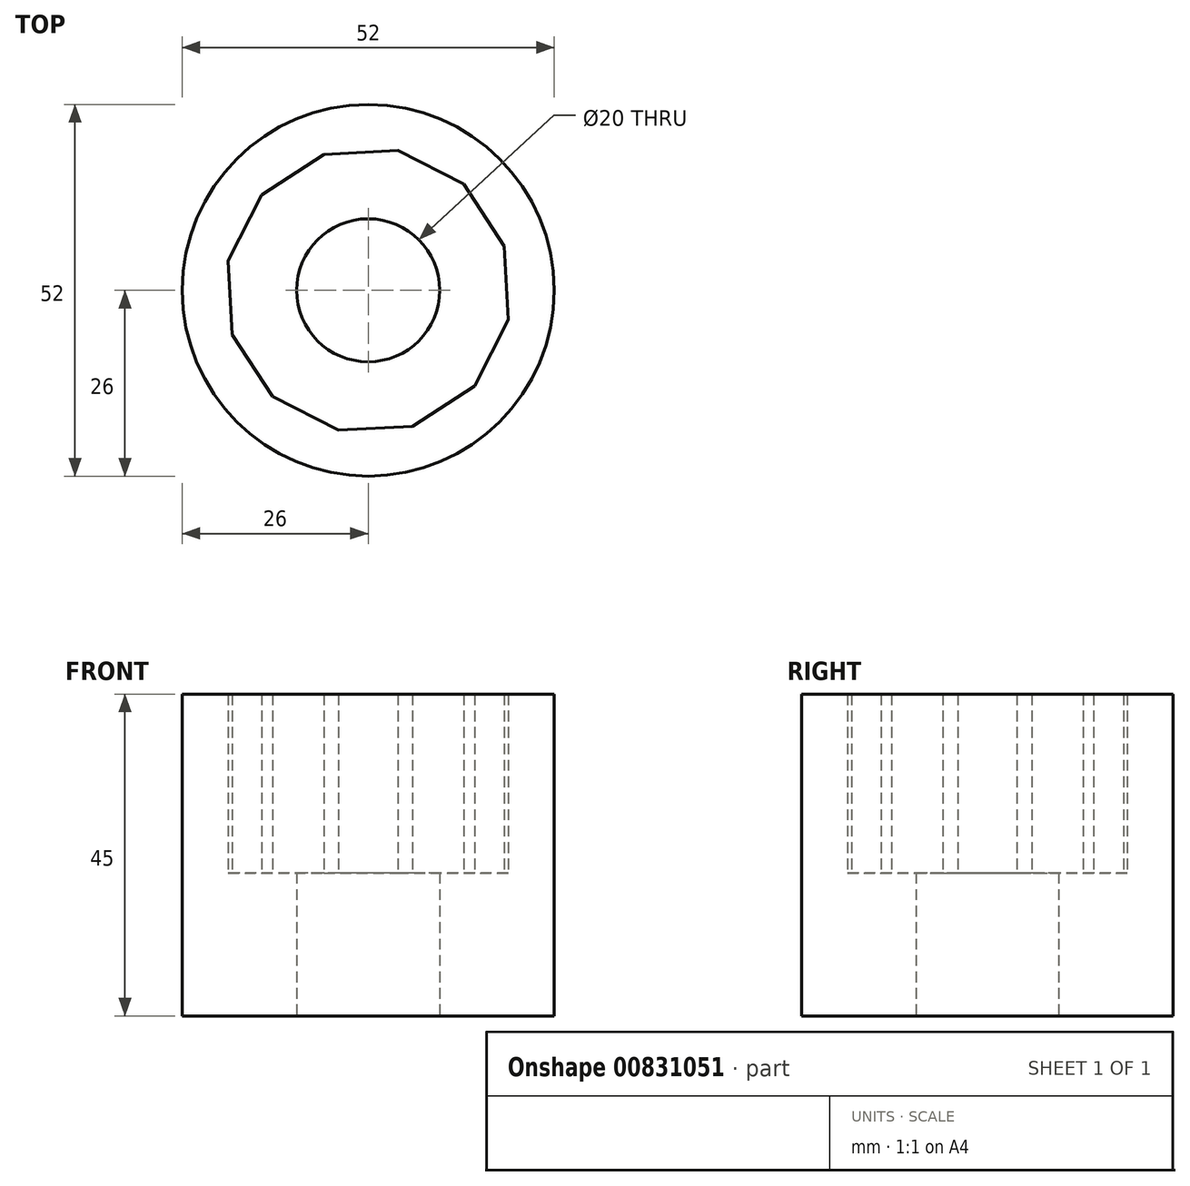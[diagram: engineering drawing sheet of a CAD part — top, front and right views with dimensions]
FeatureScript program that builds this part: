
annotation { "Feature Type Name" : "Feature", "Feature Type Description" : "" }
export const myFeature = defineFeature(function(context is Context, id is Id, definition is map)
    precondition{}
    {
        {
            var Q0;
            Q0=qCreatedBy(makeId("Top.planeOp"),FACE);
            var sketch = newSketch(context, id + "F0", { "sketchPlane" : qUnion([Q0])});
            skCircle(sketch, "E0", {"center": v(0, 0) * mm, "radius": 26 * mm});
            skCircle(sketch, "E1", {"center": v(0, 0) * mm, "radius": 10 * mm});
            skSolve(sketch);
        }
        {
            var Q0;
            Q0=makeQuery(id+"F0.imprint","IMPRINT",FACE,{"disambiguationData":[TD([[makeQuery(id+"F0.imprint","IMPRINT",EDGE,{"derivedFrom":sQuery(id+"F0.wireOp",EDGE,"E0")}),1.0]])]});
            extrude(context, id + "F1", {"entities" : qUnion([Q0]), "depth" : 20 * mm, "offsetDistance" : 25 * mm});
        }
        {
            var Q0;
            Q0=makeQuery(id+"F1.opExtrude","CAP_FACE",FACE,{"disambiguationData":[OSD([sQuery(id+"F0.wireOp",EDGE,"E0"),sQuery(id+"F0.wireOp",EDGE,"E1")])],"isStart":false});
            var sketch = newSketch(context, id + "F2", { "sketchPlane" : qUnion([Q0])});
            skCircle(sketch, "E2", {"center": v(0, 0) * mm, "radius": 20 * mm});
            skCircle(sketch, "E3", {"center": v(0, 0) * mm, "radius": 26 * mm});
            skCircle(sketch, "E4.cCircle", {"center": v(0, 0) * mm, "radius": 20 * mm, "construction": true});
            skLineSegment(sketch, "E4.0", {"start": v(13.37, 14.87) * mm, "end": v(19.02, 6.2) * mm});
            skLineSegment(sketch, "E4.1", {"start": v(19.02, 6.2) * mm, "end": v(19.57, -4.14) * mm});
            skLineSegment(sketch, "E4.2", {"start": v(19.57, -4.14) * mm, "end": v(14.87, -13.37) * mm});
            skLineSegment(sketch, "E4.3", {"start": v(14.87, -13.37) * mm, "end": v(6.2, -19.02) * mm});
            skLineSegment(sketch, "E4.4", {"start": v(6.2, -19.02) * mm, "end": v(-4.14, -19.57) * mm});
            skLineSegment(sketch, "E4.5", {"start": v(-4.14, -19.57) * mm, "end": v(-13.37, -14.87) * mm});
            skLineSegment(sketch, "E4.6", {"start": v(-13.37, -14.87) * mm, "end": v(-19.02, -6.2) * mm});
            skLineSegment(sketch, "E4.7", {"start": v(-19.02, -6.2) * mm, "end": v(-19.57, 4.14) * mm});
            skLineSegment(sketch, "E4.8", {"start": v(-19.57, 4.14) * mm, "end": v(-14.87, 13.37) * mm});
            skLineSegment(sketch, "E4.9", {"start": v(-14.87, 13.37) * mm, "end": v(-6.2, 19.02) * mm});
            skLineSegment(sketch, "E4.10", {"start": v(-6.2, 19.02) * mm, "end": v(4.14, 19.57) * mm});
            skLineSegment(sketch, "E4.11", {"start": v(4.14, 19.57) * mm, "end": v(13.37, 14.87) * mm});
            skSolve(sketch);
        }
        {
            var Q0;
            Q0=makeQuery(id+"F2.imprint","IMPRINT",FACE,{"disambiguationData":[TD([[makeQuery(id+"F2.imprint","IMPRINT",EDGE,{"derivedFrom":sQuery(id+"F2.wireOp",EDGE,"E3")}),1.0]])]});
            var Q1;
            {var subQ0=sQuery(id+"F2.wireOp",EDGE,"E4.9");Q1=makeQuery(id+"F2.imprint","IMPRINT",FACE,{"disambiguationData":[TD([[makeQuery(id+"F2.imprint","IMPRINT",EDGE,{"derivedFrom":subQ0}),1.0]])]});}
            var Q2;
            {var subQ0=sQuery(id+"F2.wireOp",EDGE,"E4.10");Q2=makeQuery(id+"F2.imprint","IMPRINT",FACE,{"disambiguationData":[TD([[makeQuery(id+"F2.imprint","IMPRINT",EDGE,{"derivedFrom":subQ0}),1.0]])]});}
            var Q3;
            {var subQ0=sQuery(id+"F2.wireOp",EDGE,"E4.11");Q3=makeQuery(id+"F2.imprint","IMPRINT",FACE,{"disambiguationData":[TD([[makeQuery(id+"F2.imprint","IMPRINT",EDGE,{"derivedFrom":subQ0}),1.0]])]});}
            var Q4;
            {var subQ0=sQuery(id+"F2.wireOp",EDGE,"E4.0");Q4=makeQuery(id+"F2.imprint","IMPRINT",FACE,{"disambiguationData":[TD([[makeQuery(id+"F2.imprint","IMPRINT",EDGE,{"derivedFrom":subQ0}),1.0]])]});}
            var Q5;
            {var subQ0=sQuery(id+"F2.wireOp",EDGE,"E4.8");Q5=makeQuery(id+"F2.imprint","IMPRINT",FACE,{"disambiguationData":[TD([[makeQuery(id+"F2.imprint","IMPRINT",EDGE,{"derivedFrom":subQ0}),1.0]])]});}
            var Q6;
            {var subQ0=sQuery(id+"F2.wireOp",EDGE,"E4.5");Q6=makeQuery(id+"F2.imprint","IMPRINT",FACE,{"disambiguationData":[TD([[makeQuery(id+"F2.imprint","IMPRINT",EDGE,{"derivedFrom":subQ0}),1.0]])]});}
            var Q7;
            {var subQ0=sQuery(id+"F2.wireOp",EDGE,"E4.6");Q7=makeQuery(id+"F2.imprint","IMPRINT",FACE,{"disambiguationData":[TD([[makeQuery(id+"F2.imprint","IMPRINT",EDGE,{"derivedFrom":subQ0}),1.0]])]});}
            var Q8;
            {var subQ0=sQuery(id+"F2.wireOp",EDGE,"E4.4");Q8=makeQuery(id+"F2.imprint","IMPRINT",FACE,{"disambiguationData":[TD([[makeQuery(id+"F2.imprint","IMPRINT",EDGE,{"derivedFrom":subQ0}),1.0]])]});}
            var Q9;
            {var subQ0=sQuery(id+"F2.wireOp",EDGE,"E4.3");Q9=makeQuery(id+"F2.imprint","IMPRINT",FACE,{"disambiguationData":[TD([[makeQuery(id+"F2.imprint","IMPRINT",EDGE,{"derivedFrom":subQ0}),1.0]])]});}
            var Q10;
            {var subQ0=sQuery(id+"F2.wireOp",EDGE,"E4.2");Q10=makeQuery(id+"F2.imprint","IMPRINT",FACE,{"disambiguationData":[TD([[makeQuery(id+"F2.imprint","IMPRINT",EDGE,{"derivedFrom":subQ0}),1.0]])]});}
            var Q11;
            {var subQ0=sQuery(id+"F2.wireOp",EDGE,"E4.1");Q11=makeQuery(id+"F2.imprint","IMPRINT",FACE,{"disambiguationData":[TD([[makeQuery(id+"F2.imprint","IMPRINT",EDGE,{"derivedFrom":subQ0}),1.0]])]});}
            var Q12;
            {var subQ0=sQuery(id+"F2.wireOp",EDGE,"E4.7");Q12=makeQuery(id+"F2.imprint","IMPRINT",FACE,{"disambiguationData":[TD([[makeQuery(id+"F2.imprint","IMPRINT",EDGE,{"derivedFrom":subQ0}),1.0]])]});}
            extrude(context, id + "F3", {"entities" : qUnion([Q0, Q1, Q2, Q3, Q4, Q5, Q6, Q7, Q8, Q9, Q10, Q11, Q12]), "operationType" : NewBodyOperationType.ADD, "depth" : 25 * mm, "offsetDistance" : 25 * mm});
        }
    });
